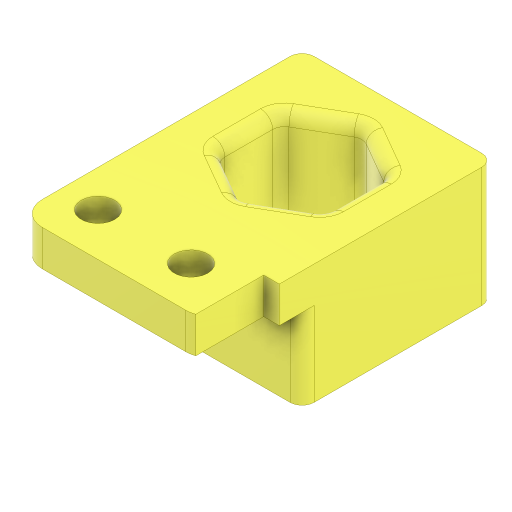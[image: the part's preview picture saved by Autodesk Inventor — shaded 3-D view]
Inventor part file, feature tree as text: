
AUTODESK INVENTOR PART (.ipt)
format: ipt  version: 2024.1 (Build 281209000, 209)  size: 252,416 bytes
history: native  units: mm
features: extrude x4, sketch x3, projected_geometry x3, other x2, fillet x1, hole x1, reference x1
ambient origin geometry x8: Origin, YZ Plane, XZ Plane, XY Plane, X Axis, Y Axis, Z Axis, Center Point
bodies: Volumenkörper1 (feature_tree)
feature tree (15):
  extrude  "Extrusion1"  Depth=16.0mm
  extrude  "Extrusion2"  Depth=8.9mm
  fillet  "Rundung2"  Radius=9.0mm
  extrude  "Extrusion3"  Depth=10.0mm
  extrude  "Extrusion4"  Depth=2.0mm
  hole  "Bohrung1"  [1 undecoded]
  sketch  "Skizze2"  dims[d0=16.0mm d1=16.0mm]
  projected_geometry  "Projizierte Kontur1"
  sketch  "Skizze3"  dims[d3=1.0mm d4=0.0mm d6=8.9mm d7=9.0mm d8=0.0mm]
  projected_geometry  "Projizierte Kontur2"
  reference  "Referenz1"
  sketch  "Skizze5"  dims[d9=1.0mm d10=10.0mm d11=2.8mm d12=2.8mm d13=2.0mm d14=3.0mm d15=0.0mm d16=0.1mm d17=0.0mm d18=0.0mm d19=9.5mm d20=9.5mm d21=6.0mm d22=9.5mm d23=9.5mm d24=1.8mm d25=1.8mm d26=1.8mm d27=1.8mm d28=2.0mm d29=6.0mm d30=4.0mm d31=2.0mm d32=90.0deg d33=8.0mm d34=150.0deg]
  projected_geometry  "Projizierte Kontur3"
  other  "Assemlby_lightsheet_generator_passive_v2.iam"
  other  "30_Lightsheet_generator_passive_lid_v1:1"
note: 1 required parameter value undecoded (feature->parameter linkage not recoverable at this tier; creation-order binding heuristic only, values carry confidence <= 0.55)
